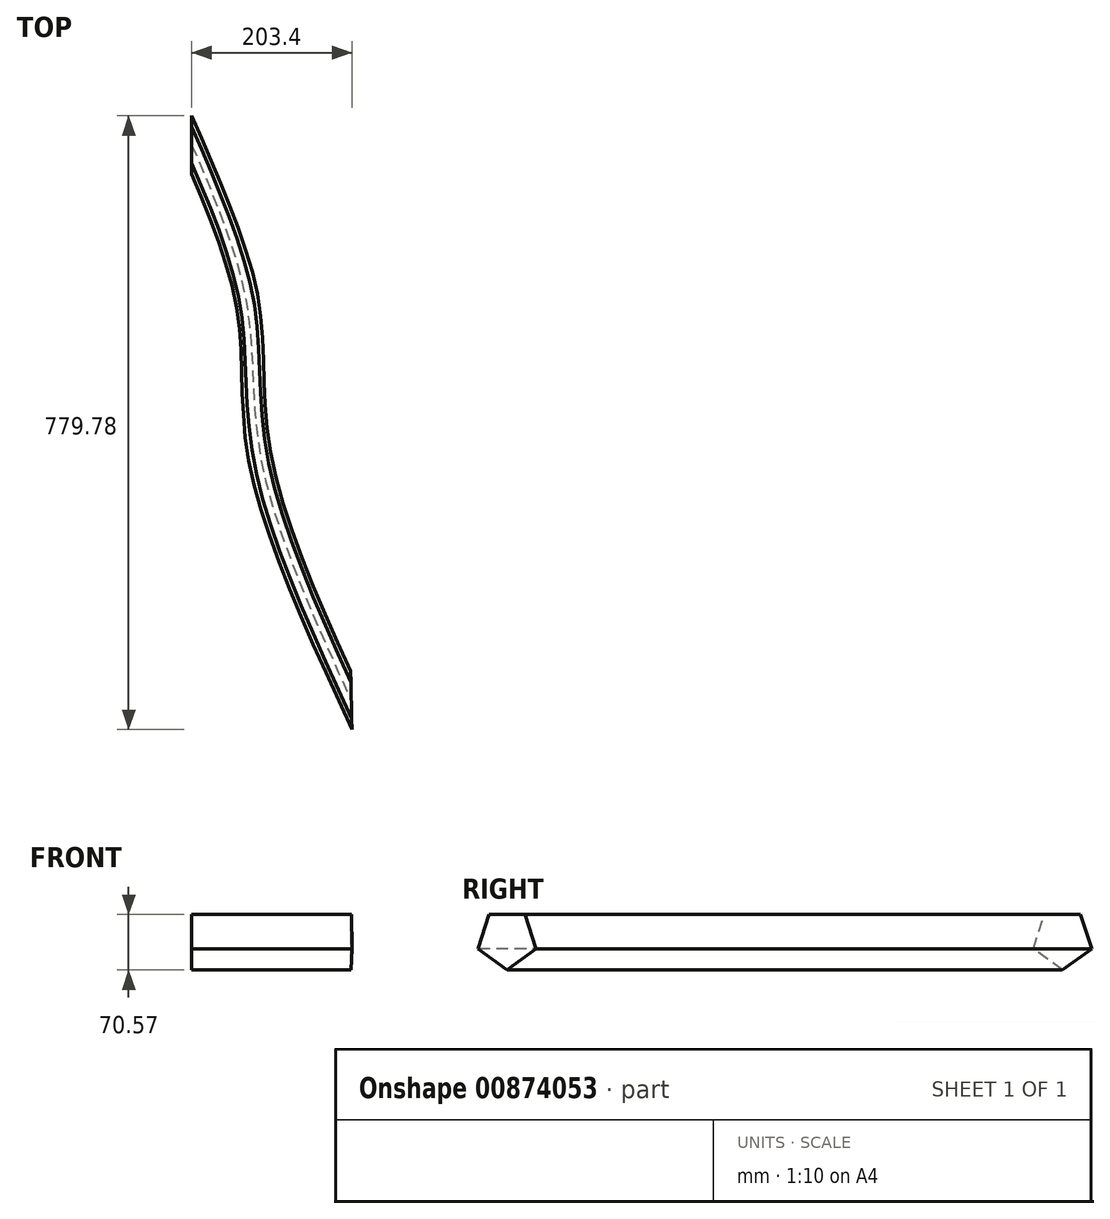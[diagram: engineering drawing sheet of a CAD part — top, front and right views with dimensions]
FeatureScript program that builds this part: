
annotation { "Feature Type Name" : "Feature", "Feature Type Description" : "" }
export const myFeature = defineFeature(function(context is Context, id is Id, definition is map)
    precondition{}
    {
        {
            var Q0;
            Q0=qCreatedBy(makeId("Right.planeOp"),FACE);
            var sketch = newSketch(context, id + "F0", { "sketchPlane" : qUnion([Q0])});
            skCircle(sketch, "E0.cCircle", {"center": v(0, 0) * mm, "radius": 31.56 * mm, "construction": true});
            skLineSegment(sketch, "E0.0", {"start": v(-22.93, 31.56) * mm, "end": v(22.93, 31.56) * mm});
            skLineSegment(sketch, "E0.1", {"start": v(22.93, 31.56) * mm, "end": v(37.1, -12.05) * mm});
            skLineSegment(sketch, "E0.2", {"start": v(37.1, -12.05) * mm, "end": v(0, -39) * mm});
            skLineSegment(sketch, "E0.3", {"start": v(0, -39) * mm, "end": v(-37.1, -12.05) * mm});
            skLineSegment(sketch, "E0.4", {"start": v(-37.1, -12.05) * mm, "end": v(-22.93, 31.56) * mm});
            skPoint(sketch, "E0.0.midPoint", {"position": v(0, 31.56) * mm});
            skSolve(sketch);
        }
        {
            var Q0;
            Q0=qCreatedBy(makeId("Top.planeOp"),FACE);
            var sketch = newSketch(context, id + "F1", { "sketchPlane" : qUnion([Q0])});
            skFitSpline(sketch, "E1", {"points": [v(0, 0) * mm, v(69.99, -203.9) * mm, v(87.81, -398.7) * mm, v(202.58, -705.6) * mm], "startDerivative": vector(281.08, -657.3) * mm, "endDerivative": vector(379, -834.97) * mm});
            skSolve(sketch);
        }
        {
            var Q0;
            Q0=makeQuery(id+"F0.imprint","IMPRINT",FACE,{"disambiguationData":[TD([[makeQuery(id+"F0.imprint","IMPRINT",EDGE,{"derivedFrom":sQuery(id+"F0.wireOp",EDGE,"E0.0")}),-1.0]])]});
            var Q1;
            Q1=sQuery(id+"F1.wireOp",EDGE,"E1");
            sweep(context, id + "F2", {"profiles" : qUnion([Q0]), "path" : qUnion([Q1])});
        }
    });
